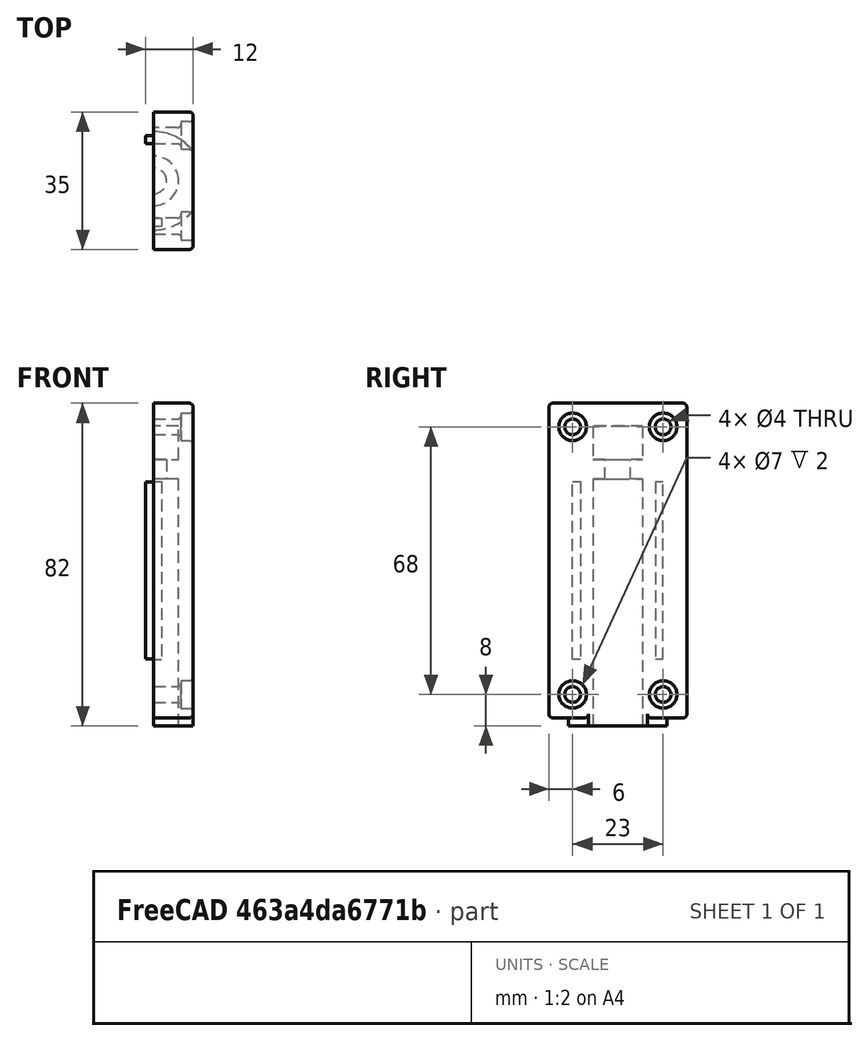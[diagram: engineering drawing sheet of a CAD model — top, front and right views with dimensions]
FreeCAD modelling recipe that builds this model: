
FCSTD DOCUMENT  (FreeCAD 0.21R33771 (Git))
Label: OlabilWheelAttachement
License: All rights reserved
LicenseURL: http://en.wikipedia.org/wiki/All_rights_reserved
objects: Sketcher::SketchObject×8, PartDesign::Pad×4, PartDesign::Pocket×4, PartDesign::Body×2, PartDesign::Fillet×1, Part::Cut×1, Mesh::Feature×1
note: 29 computed .brp shape members not serialized (recipe doc carries the construction recipe); baked Part::Feature solids carry a one-line shape summary decoded from their .brp

FEATURE [Sketcher::SketchObject] Sketch001  label="PinBaseSketch"
  FullyConstrained = true
  MapMode = 2
  Support = -> [XY_Plane]
  sketch-geometry (1):
    g0: Circle CenterX=0 CenterY=0 CenterZ=0 NormalX=0 NormalY=0 NormalZ=1 AngleXU=0 Radius=6.3
  constraints (2):
    c: Coincident(g0,g-1)
    c: Diameter(g0) = 12.6
FEATURE [PartDesign::Pad] Pad001  label="PinBasePad"
  Direction = (0,0,1)
  Length = 76.2
  Length2 = 10
  Profile = -> Sketch001
  ReferenceAxis = -> Sketch001 [N_Axis]
  Type = 0
FEATURE [Sketcher::SketchObject] Sketch002  label="PinScoreSketch"
  AttachmentOffset = pos=(0,0,67.7) rot=(0,0,1;0rad)
  FullyConstrained = true
  MapMode = 5
  Placement = pos=(0,0,67.7) rot=(0,0,1;0rad)
  Support = -> [XY_Plane]
  sketch-geometry (2):
    g0: Circle CenterX=0 CenterY=0 CenterZ=0 NormalX=0 NormalY=0 NormalZ=1 AngleXU=0 Radius=6.3
    g1: Circle CenterX=0 CenterY=0 CenterZ=0 NormalX=0 NormalY=0 NormalZ=1 AngleXU=0 Radius=3.25
  constraints (4):
    c: Coincident(g0,g-1)
    c: Coincident(g1,g0)
    c: Diameter(g1) = 6.5
    c: Diameter(g0) = 12.6
FEATURE [PartDesign::Pocket] Pocket  label="PinScorePocket"
  BaseFeature = -> Pad001
  Direction = (0,0,-1)
  Length = 5
  Length2 = 5
  Profile = -> Sketch002
  ReferenceAxis = -> Sketch002 [N_Axis]
  Type = 0
FEATURE [PartDesign::Body] Body  label="PinBody"
  Group = -> [Sketch001,Pad001,Sketch002,Pocket]
  Origin = -> Origin
  Tip = -> Pocket
FEATURE [Sketcher::SketchObject] Sketch  label="BoxBodySketch"
  FullyConstrained = true
  MapMode = 5
  Placement = pos=(0,0,0) rot=(0.57735,0.57735,0.57735;2.0944rad)
  Support = -> [YZ_Plane001]
  sketch-geometry (4):
    g0: LineSegment StartX=-17.5 StartY=82 StartZ=0 EndX=17.5 EndY=82 EndZ=0
    g1: LineSegment StartX=17.5 StartY=82 StartZ=0 EndX=17.5 EndY=2 EndZ=0
    g2: LineSegment StartX=17.5 StartY=2 StartZ=0 EndX=-17.5 EndY=2 EndZ=0
    g3: LineSegment StartX=-17.5 StartY=2 StartZ=0 EndX=-17.5 EndY=82 EndZ=0
  constraints (11):
    c: Coincident(g0,g1)
    c: Coincident(g1,g2)
    c: Coincident(g2,g3)
    c: Coincident(g3,g0)
    c: Horizontal(g2)
    c: Vertical(g1)
    c: Vertical(g3)
    c: Symmetric(g0,g0,g-2)
    c: DistanceY(g-1,g1) = 2
    c: DistanceY(g1,g1) = 80
    c: DistanceX(g0,g0) = 35
FEATURE [PartDesign::Pad] Pad  label="BoxBodyPad"
  Direction = (1,-2e-16,3e-16)
  Length = 10
  Length2 = 10
  Placement = pos=(0,0,0) rot=(1,1,1;2.0944rad)
  Profile = -> Sketch
  ReferenceAxis = -> Sketch [N_Axis]
  Type = 0
FEATURE [Sketcher::SketchObject] Sketch003  label="BearingSupportSketch"
  ExternalGeometry = -> [Pad]
  FullyConstrained = true
  MapMode = 5
  Placement = pos=(-8e-16,1.1e-15,2) rot=(0.707107,0.707107,0;3.14159rad)
  Support = -> [Pad]
  sketch-geometry (4):
    g0: LineSegment StartX=-12.5 StartY=1.5e-15 StartZ=0 EndX=12.5 EndY=0 EndZ=0
    g1: ArcOfCircle CenterX=0 CenterY=0 CenterZ=0 NormalX=0 NormalY=0 NormalZ=1 AngleXU=0 Radius=12.5 StartAngle=0 EndAngle=0.927295
    g2: ArcOfCircle CenterX=0 CenterY=0 CenterZ=0 NormalX=0 NormalY=0 NormalZ=1 AngleXU=0 Radius=12.5 StartAngle=2.2143 EndAngle=3.14159
    g3: LineSegment StartX=-7.5 StartY=10 StartZ=0 EndX=7.5 EndY=10 EndZ=0
  constraints (11):
    c: Coincident(g1,g-1)
    c: PointOnObject(g1,g-1)
    c: Coincident(g0,g2)
    c: Coincident(g0,g1)
    c: Diameter(g1) = 25
    c: PointOnObject(g1,g-3)
    c: Coincident(g2,g1)
    c: Symmetric(g2,g1,g-2)
    c: PointOnObject(g1,g0)
    c: Coincident(g3,g2)
    c: Coincident(g3,g1)
FEATURE [PartDesign::Pad] Pad002  label="BearingSupportPad"
  BaseFeature = -> Pad
  Direction = (4e-16,-6e-16,-1)
  Length = 2
  Length2 = 10
  Placement = pos=(0,0,0) rot=(1,1,1;2.0944rad)
  Profile = -> Sketch003
  ReferenceAxis = -> Sketch003 [N_Axis]
  Type = 0
FEATURE [Sketcher::SketchObject] Sketch004  label="AlignmentBumpSketch"
  ExternalGeometry = -> [Pad002]
  FullyConstrained = true
  MapMode = 5
  Placement = pos=(-1.87e-14,0,0) rot=(-0.57735,-0.57735,0.57735;2.0944rad)
  Support = -> [Pad002]
  sketch-geometry (4):
    g0: LineSegment StartX=9.5 StartY=-17 StartZ=0 EndX=11.5 EndY=-17 EndZ=0
    g1: LineSegment StartX=11.5 StartY=-17 StartZ=0 EndX=11.5 EndY=-62 EndZ=0
    g2: LineSegment StartX=11.5 StartY=-62 StartZ=0 EndX=9.5 EndY=-62 EndZ=0
    g3: LineSegment StartX=9.5 StartY=-62 StartZ=0 EndX=9.5 EndY=-17 EndZ=0
  constraints (12):
    c: Coincident(g0,g1)
    c: Coincident(g1,g2)
    c: Coincident(g2,g3)
    c: Coincident(g3,g0)
    c: Horizontal(g0)
    c: Horizontal(g2)
    c: Vertical(g1)
    c: Vertical(g3)
    c: DistanceX(g0,g0) = 2
    c: DistanceY(g3,g3) = 45
    c: DistanceY(g0,g-4) = 15
    c: DistanceX(g0,g-3) = 8
FEATURE [PartDesign::Pad] Pad003  label="AllignmentBumpPad"
  BaseFeature = -> Pad002
  Direction = (-1,6e-16,-5e-16)
  Length = 2
  Length2 = 10
  Placement = pos=(0,0,0) rot=(1,1,1;2.0944rad)
  Profile = -> Sketch004
  ReferenceAxis = -> Sketch004 [N_Axis]
  Type = 0
FEATURE [Sketcher::SketchObject] Sketch005  label="AllignmentDumpSketch"
  ExternalGeometry = -> [Pad003]
  FullyConstrained = true
  MapMode = 5
  Placement = pos=(-2.8e-14,0,0) rot=(-0.57735,-0.57735,0.57735;2.0944rad)
  Support = -> [Pad003]
  sketch-geometry (6):
    g0: GeomPoint X=10.5 Y=-39.5 Z=0
    g1: LineSegment StartX=-11.55 StartY=-16.9 StartZ=0 EndX=-11.55 EndY=-62.1 EndZ=0
    g2: LineSegment StartX=-11.55 StartY=-62.1 StartZ=0 EndX=-9.45 EndY=-62.1 EndZ=0
    g3: LineSegment StartX=-9.45 StartY=-62.1 StartZ=0 EndX=-9.45 EndY=-16.9 EndZ=0
    g4: LineSegment StartX=-9.45 StartY=-16.9 StartZ=0 EndX=-11.55 EndY=-16.9 EndZ=0
    g5: GeomPoint X=-10.5 Y=-39.5 Z=0
  constraints (13):
    c: Symmetric(g-6,g-5,g0)
    c: Coincident(g1,g2)
    c: Coincident(g2,g3)
    c: Coincident(g3,g4)
    c: Coincident(g4,g1)
    c: Horizontal(g2)
    c: Horizontal(g4)
    c: Vertical(g1)
    c: Vertical(g3)
    c: Symmetric(g2,g1,g5)
    c: Symmetric(g5,g0,g-2)
    c: DistanceY(g-4,g3) = 0.1
    c: DistanceX(g2,g2) = 2.1
FEATURE [PartDesign::Pocket] Pocket001  label="AllignmentDumpPocket"
  BaseFeature = -> Pad003
  Direction = (1,-8e-16,7e-16)
  Length = 2
  Length2 = 5
  Placement = pos=(0,0,0) rot=(1,1,1;2.0944rad)
  Profile = -> Sketch005
  ReferenceAxis = -> Sketch005 [N_Axis]
  Type = 0
FEATURE [Sketcher::SketchObject] Sketch006  label="SkrewHolesSketch"
  ExternalGeometry = -> [Pocket001]
  FullyConstrained = true
  MapMode = 5
  Placement = pos=(10,-1.11e-14,6.7e-15) rot=(0.57735,0.57735,0.57735;2.0944rad)
  Support = -> [Pocket001]
  expr: Constraints[8] = .Constraints.offset
  expr: Constraints[9] = .Constraints.offset
  sketch-geometry (4):
    g0: Circle CenterX=-11.5 CenterY=76 CenterZ=0 NormalX=0 NormalY=0 NormalZ=1 AngleXU=0 Radius=2
    g1: Circle CenterX=11.5 CenterY=76 CenterZ=0 NormalX=0 NormalY=0 NormalZ=1 AngleXU=0 Radius=2
    g2: Circle CenterX=11.5 CenterY=8 CenterZ=0 NormalX=0 NormalY=0 NormalZ=1 AngleXU=0 Radius=2
    g3: Circle CenterX=-11.5 CenterY=8 CenterZ=0 NormalX=0 NormalY=0 NormalZ=1 AngleXU=0 Radius=2
  constraints (11):
    c: Equal(g0,g1)
    c: Equal(g0,g2)
    c: Equal(g0,g3)
    c: Diameter(g0) = 4
    c: Horizontal(g3,g2)
    c: Vertical(g0,g3)
    c: Vertical(g1,g2)
    c: Symmetric(g0,g1,g-2)
    c: DistanceY(g0,g-3) = 6
    c: DistanceX(g-6,g3) = 6
    c: DistanceY(g-6,g3) = 6  'offset'
FEATURE [PartDesign::Pocket] Pocket002  label="SkrewHoles"
  BaseFeature = -> Pocket001
  Direction = (-1,1.1e-15,-7e-16)
  Length = 5
  Length2 = 5
  Placement = pos=(0,0,0) rot=(1,1,1;2.0944rad)
  Profile = -> Sketch006
  ReferenceAxis = -> Sketch006 [N_Axis]
  Type = 1
FEATURE [Sketcher::SketchObject] Sketch007  label="SkrewBrimSketch"
  ExternalGeometry = -> [Pocket002]
  FullyConstrained = true
  MapMode = 5
  Placement = pos=(10,-1.33e-14,7.8e-15) rot=(0.57735,0.57735,0.57735;2.0944rad)
  Support = -> [Pocket002]
  sketch-geometry (4):
    g0: Circle CenterX=-11.5 CenterY=76 CenterZ=0 NormalX=0 NormalY=0 NormalZ=1 AngleXU=0 Radius=3.5
    g1: Circle CenterX=11.5 CenterY=76 CenterZ=0 NormalX=0 NormalY=0 NormalZ=1 AngleXU=0 Radius=3.5
    g2: Circle CenterX=11.5 CenterY=8 CenterZ=0 NormalX=0 NormalY=0 NormalZ=1 AngleXU=0 Radius=3.5
    g3: Circle CenterX=-11.5 CenterY=8 CenterZ=0 NormalX=0 NormalY=0 NormalZ=1 AngleXU=0 Radius=3.5
  constraints (8):
    c: Coincident(g0,g-4)
    c: Coincident(g1,g-3)
    c: Coincident(g2,g-6)
    c: Coincident(g3,g-5)
    c: Equal(g3,g0)
    c: Equal(g3,g1)
    c: Equal(g3,g2)
    c: Diameter(g3) = 7
FEATURE [PartDesign::Pocket] Pocket003  label="SkrewBrimPocket"
  BaseFeature = -> Pocket002
  Direction = (-1,1.3e-15,-9e-16)
  Length = 3
  Length2 = 5
  Placement = pos=(0,0,0) rot=(1,1,1;2.0944rad)
  Profile = -> Sketch007
  ReferenceAxis = -> Sketch007 [N_Axis]
  Type = 0
FEATURE [PartDesign::Fillet] Fillet
  Base = -> Pocket003 [Edge5,Edge1,Edge2,Edge8,Edge7,Edge26,Edge27,Edge10,Edge4,Edge30,Edge29,Edge31,Edge32,Edge48,Edge38,Edge50,Edge60]
  BaseFeature = -> Pocket003
  Placement = pos=(0,0,0) rot=(1,1,1;2.0944rad)
  Radius = 1
  SupportTransform = false
  UseAllEdges = false
FEATURE [PartDesign::Body] Body001  label="PartBody"
  Group = -> [Sketch,Pad,Sketch003,Pad002,Sketch004,Pad003,Sketch005,Pocket001,Sketch006,Pocket002,Sketch007,Pocket003,Fillet]
  Origin = -> Origin001
  Tip = -> Fillet
FEATURE [Part::Cut] Cut  label="OlabilWheelCoupler"
  Base = -> Body001
  Tool = -> Body
FEATURE [Mesh::Feature] Mesh  label="OlabilWheelCoupler (Meshed)"
